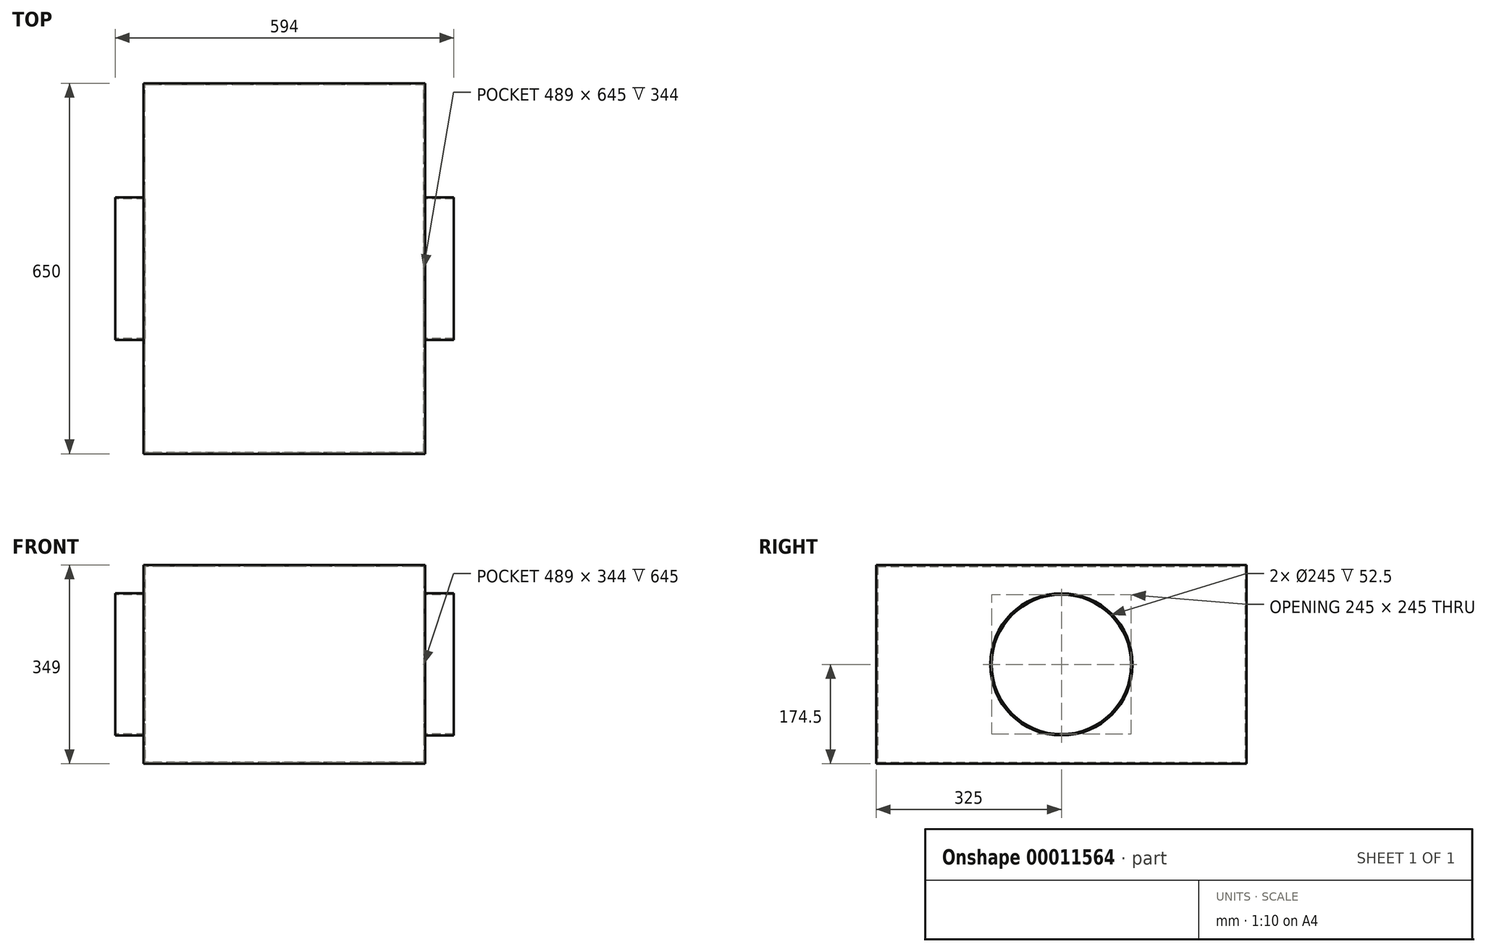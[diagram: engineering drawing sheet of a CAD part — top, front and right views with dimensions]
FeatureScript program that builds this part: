
annotation { "Feature Type Name" : "Feature", "Feature Type Description" : "" }
export const myFeature = defineFeature(function(context is Context, id is Id, definition is map)
    precondition{}
    {
        {
            var Q0;
            Q0=qCreatedBy(makeId("Top.planeOp"),FACE);
            var sketch = newSketch(context, id + "F0", { "sketchPlane" : qUnion([Q0])});
            skLineSegment(sketch, "E0.rect.bottom", {"start": v(247, -325) * mm, "end": v(-247, -325) * mm});
            skLineSegment(sketch, "E0.rect.top", {"start": v(247, 325) * mm, "end": v(-247, 325) * mm});
            skLineSegment(sketch, "E0.rect.left", {"start": v(247, -325) * mm, "end": v(247, 325) * mm});
            skLineSegment(sketch, "E0.rect.right", {"start": v(-247, -325) * mm, "end": v(-247, 325) * mm});
            skPoint(sketch, "E0.rect.middle", {"position": v(0, 0) * mm});
            skSolve(sketch);
        }
        {
            var Q0;
            Q0=makeQuery(id+"F0.imprint","IMPRINT",FACE,{"disambiguationData":[TD([[makeQuery(id+"F0.imprint","IMPRINT",EDGE,{"derivedFrom":sQuery(id+"F0.wireOp",EDGE,"E0.rect.bottom")}),-1.0]])]});
            extrude(context, id + "F1", {"entities" : qUnion([Q0]), "endBound" : BoundingType.SYMMETRIC, "depth" : 349 * mm});
        }
        {
            var Q0;
            Q0=qCreatedBy(makeId("Right.planeOp"),FACE);
            var sketch = newSketch(context, id + "F2", { "sketchPlane" : qUnion([Q0])});
            skCircle(sketch, "E1", {"center": v(0, 0) * mm, "radius": 125 * mm});
            skSolve(sketch);
        }
        {
            var Q0;
            Q0 = qSketchRegion(id + "F2", true);
            extrude(context, id + "F3", {"entities" : qUnion([Q0]), "operationType" : NewBodyOperationType.ADD, "endBound" : BoundingType.SYMMETRIC, "depth" : 594 * mm});
        }
        {
            var Q0;
            Q0=makeQuery(id+"F3.opExtrude","CAP_FACE",FACE,{"disambiguationData":[OSD([sQuery(id+"F2.wireOp",EDGE,"E1")])],"isStart":false});
            var Q1;
            Q1=makeQuery(id+"F3.opExtrude","CAP_FACE",FACE,{"disambiguationData":[OSD([sQuery(id+"F2.wireOp",EDGE,"E1")])],"isStart":true});
            shell(context, id + "F4", {"entities" : qUnion([Q0, Q1]), "thickness" : 2.5 * mm});
        }
    });
